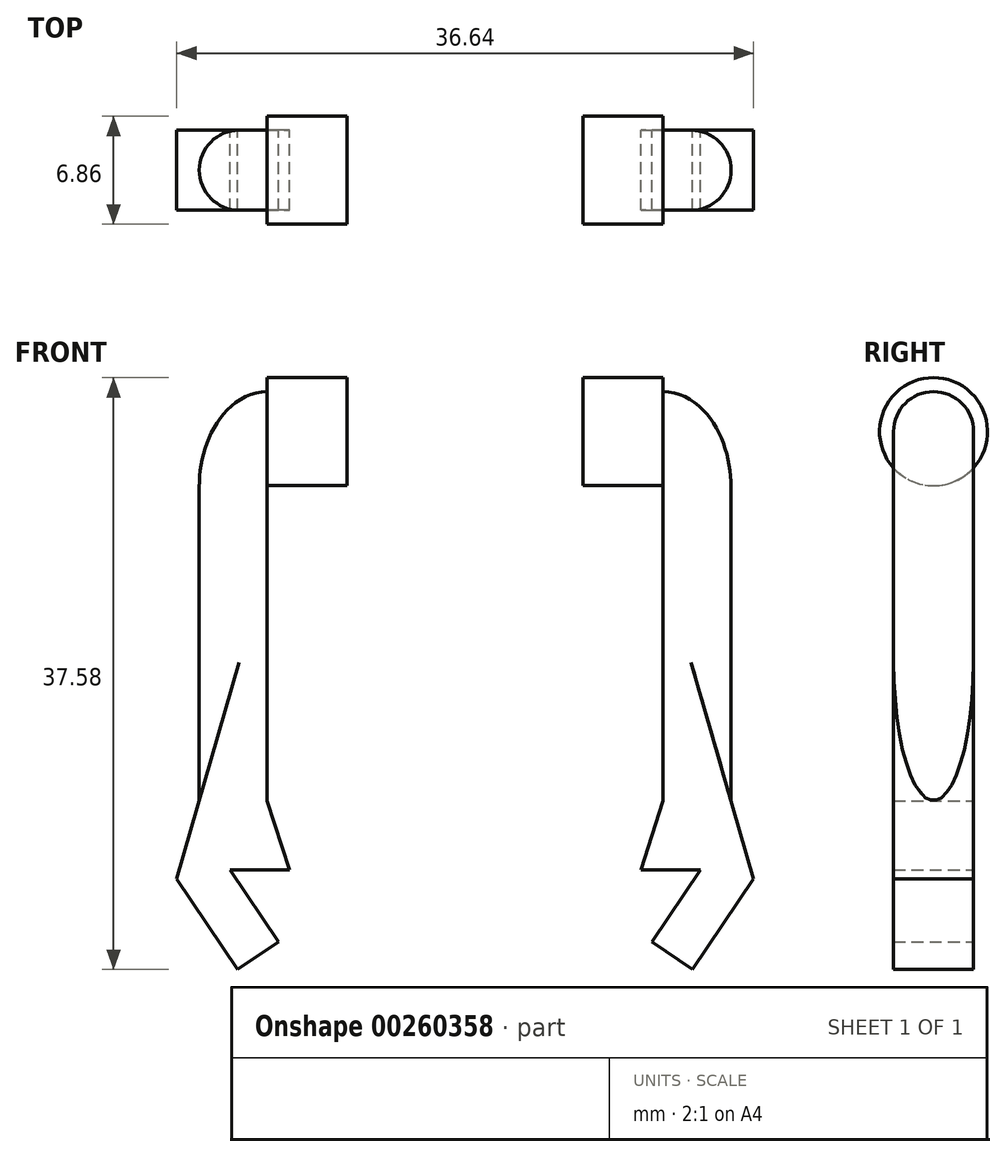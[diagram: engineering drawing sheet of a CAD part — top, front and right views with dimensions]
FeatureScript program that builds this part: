
annotation { "Feature Type Name" : "Feature", "Feature Type Description" : "" }
export const myFeature = defineFeature(function(context is Context, id is Id, definition is map)
    precondition{}
    {
        {
            var Q0;
            Q0=qCreatedBy(makeId("Front.planeOp"),FACE);
            var sketch = newSketch(context, id + "F0", { "sketchPlane" : qUnion([Q0])});
            skLineSegment(sketch, "E0", {"start": v(-16.89, 30.63) * mm, "end": v(-12.57, 30.63) * mm});
            skLineSegment(sketch, "E1", {"start": v(-12.57, 30.63) * mm, "end": v(-12.57, 36.7) * mm});
            skLineSegment(sketch, "E2.top", {"start": v(-16.89, 10.7) * mm, "end": v(-12.57, 10.7) * mm});
            skLineSegment(sketch, "E2.left", {"start": v(-16.89, 30.63) * mm, "end": v(-16.89, 10.7) * mm});
            skLineSegment(sketch, "E2.right", {"start": v(-12.57, 30.63) * mm, "end": v(-12.57, 10.7) * mm});
            skPoint(sketch, "E3", {"position": v(0, 22.5) * mm});
            skEllipticalArc(sketch, "E4", {});
            skLineSegment(sketch, "E5.MirrorCS", {"start": v(16.89, 30.63) * mm, "end": v(12.57, 30.63) * mm});
            skLineSegment(sketch, "E6.MirrorCS", {"start": v(12.57, 30.63) * mm, "end": v(12.57, 36.7) * mm});
            skLineSegment(sketch, "E7.MirrorCS", {"start": v(16.89, 10.7) * mm, "end": v(12.57, 10.7) * mm});
            skLineSegment(sketch, "E8.MirrorCS", {"start": v(12.57, 30.63) * mm, "end": v(12.57, 10.7) * mm});
            skLineSegment(sketch, "E9.MirrorCS", {"start": v(16.89, 30.63) * mm, "end": v(16.89, 10.7) * mm});
            skEllipticalArc(sketch, "E10.MirrorCS", {});
            skLineSegment(sketch, "E11", {"start": v(-16.89, 10.7) * mm, "end": v(-18.32, 5.75) * mm});
            skLineSegment(sketch, "E12", {"start": v(-18.32, 5.75) * mm, "end": v(-14.45, 0) * mm});
            skLineSegment(sketch, "E13", {"start": v(-14.45, 0) * mm, "end": v(-11.86, 1.74) * mm});
            skLineSegment(sketch, "E14", {"start": v(-11.86, 1.74) * mm, "end": v(-14.94, 6.33) * mm});
            skLineSegment(sketch, "E15", {"start": v(-14.94, 6.33) * mm, "end": v(-11.16, 6.33) * mm});
            skLineSegment(sketch, "E16", {"start": v(-11.16, 6.33) * mm, "end": v(-12.57, 10.7) * mm});
            skLineSegment(sketch, "E17.MirrorCS", {"start": v(11.86, 1.74) * mm, "end": v(14.94, 6.33) * mm});
            skLineSegment(sketch, "E18.MirrorCS", {"start": v(14.94, 6.33) * mm, "end": v(11.16, 6.33) * mm});
            skLineSegment(sketch, "E19.MirrorCS", {"start": v(11.16, 6.33) * mm, "end": v(12.57, 10.7) * mm});
            skLineSegment(sketch, "E20.MirrorCS", {"start": v(16.89, 10.7) * mm, "end": v(18.32, 5.75) * mm});
            skLineSegment(sketch, "E21.MirrorCS", {"start": v(18.32, 5.75) * mm, "end": v(14.45, 0) * mm});
            skLineSegment(sketch, "E22.MirrorCS", {"start": v(14.45, 0) * mm, "end": v(11.86, 1.74) * mm});
            const initialGuessF0  = {"E4": [-0.012565945275127886, 0.030628471164045424, 0, 1, 0.006065334670219245, 0.00432298984378576, 0, 1.5707963267948963], "E10.MirrorCS": [0.012565945275127886, 0.030628471164045424, 0, 1, 0.006065334670219245, 0.00432298984378576, 4.71238898038469, 0]};
            skSetInitialGuess(sketch, initialGuessF0);
            skSolve(sketch);
        }
        {
            var Q0;
            Q0 = qSketchRegion(id + "F0", true);
            extrude(context, id + "F1", {"entities" : qUnion([Q0]), "depth" : 5.08 * mm});
        }
        {
            var Q0;
            Q0=makeQuery(id+"F1.opExtrude","CAP_EDGE",EDGE,{"disambiguationData":[OSD([sQuery(id+"F0.wireOp",EDGE,"E2.left")])],"isStart":false});
            fillet(context, id + "F2", {"entities" : qUnion([Q0]), "radius" : 2.54 * mm, "tangentPropagation" : true, "allowEdgeOverflow" : false});
        }
        {
            var Q0;
            Q0=makeQuery(id+"F1.opExtrude","CAP_EDGE",EDGE,{"disambiguationData":[OSD([sQuery(id+"F0.wireOp",EDGE,"E2.left")])],"isStart":true});
            fillet(context, id + "F3", {"entities" : qUnion([Q0]), "radius" : 2.54 * mm, "tangentPropagation" : true, "allowEdgeOverflow" : false});
        }
        {
            var Q0;
            Q0=makeQuery(id+"F1.opExtrude","CAP_EDGE",EDGE,{"disambiguationData":[OSD([sQuery(id+"F0.wireOp",EDGE,"E9.MirrorCS")])],"isStart":false});
            var Q1;
            Q1=makeQuery(id+"F1.opExtrude","CAP_EDGE",EDGE,{"disambiguationData":[OSD([sQuery(id+"F0.wireOp",EDGE,"E9.MirrorCS")])],"isStart":true});
            fillet(context, id + "F4", {"entities" : qUnion([Q0, Q1]), "radius" : 2.54 * mm, "tangentPropagation" : true, "allowEdgeOverflow" : false});
        }
        {
            var Q0;
            Q0=makeQuery(id+"F1.opExtrude","SWEPT_FACE",FACE,{"disambiguationData":[OSD([sQuery(id+"F0.wireOp",EDGE,"E1"),sQuery(id+"F0.wireOp",EDGE,"E2.right")])]});
            var sketch = newSketch(context, id + "F5", { "sketchPlane" : qUnion([Q0])});
            skCircle(sketch, "E23", {"center": v(-2.54, 34.15) * mm, "radius": 3.43 * mm});
            skSolve(sketch);
        }
        {
            var Q0;
            Q0 = qSketchRegion(id + "F5", true);
            extrude(context, id + "F6", {"entities" : qUnion([Q0]), "operationType" : NewBodyOperationType.ADD, "depth" : 5.08 * mm});
        }
        {
            var Q0;
            Q0=makeQuery(id+"F1.opExtrude","SWEPT_FACE",FACE,{"disambiguationData":[OSD([sQuery(id+"F0.wireOp",EDGE,"E6.MirrorCS"),sQuery(id+"F0.wireOp",EDGE,"E8.MirrorCS")])]});
            var sketch = newSketch(context, id + "F7", { "sketchPlane" : qUnion([Q0])});
            skCircle(sketch, "E24", {"center": v(2.54, 34.15) * mm, "radius": 2.54 * mm});
            skSolve(sketch);
        }
        {
            var Q0;
            {var subQ0=sQuery(id+"F7.wireOp",EDGE,"E24");var subQ1=makeQuery(id+"F7.imprint","IMPRINT",VERTEX,{"derivedFrom":subQ0});Q0=makeQuery(id+"F7.imprint","IMPRINT",FACE,{"disambiguationData":[TD([[makeQuery(id+"F7.imprint","IMPRINT",EDGE,{"disambiguationData":[TD([[subQ1,-1.0]])],"derivedFrom":subQ0}),1.0]])]});}
            extrude(context, id + "F8", {"entities" : qUnion([Q0]), "operationType" : NewBodyOperationType.ADD, "depth" : 5.08 * mm});
        }
        {
            var Q0;
            Q0=makeQuery(id+"F1.opExtrude","SWEPT_BODY",BODY,{"disambiguationData":[OSD([sQuery(id+"F0.wireOp",EDGE,"E1"),sQuery(id+"F0.wireOp",EDGE,"E2.top"),sQuery(id+"F0.wireOp",EDGE,"E2.left"),sQuery(id+"F0.wireOp",EDGE,"E2.right"),sQuery(id+"F0.wireOp",EDGE,"E4")])]});
            var Q1;
            Q1=qCreatedBy(makeId("Right.planeOp"),FACE);
            mirror(context, id + "F9", {"operationType" : NewBodyOperationType.ADD, "entities" : qUnion([Q0]), "mirrorPlane" : qUnion([Q1])});
        }
    });
